# Revit family: Domotics-DomesticRanges-GEWISS-CHORUS_COMMAND-TWO-WAY_SWITCH_3M
name_source: partatom
category: Apparecchi elettrici
revit_build: Autodesk Revit 2016 (Build: 20161004_0715(x64)
units: mm (PartAtom-declared; Revit-internal decimal feet)

## family parameters
Condiviso = Sì
Host = Superficie
Mantenere orientamento annotazione = Sì
Numero OmniClass = 23.80.50.11.14
Punto di calcolo locali = No
Quota connettore circolare = Usa diametro
Taglio con vuoti quando caricato = Sì
Tipo di parte = Normale
Titolo OmniClass = Switches

## types (9) — shared parameters
Bidimensionale = bidimensionale deviatori 3m : GW12083
Breaking capacity: = 1.25 In (200 position changes)
Carico apparente = 0 VA
Catalogue = DOMOTICS
Catalogue Range = CHORUS - DOMESTIC RANGE
Category = Two-way switch
Electrocod = 0130
Glow Wire Test = 850°C
IDF = d9a2dc52-6f96-4b1c-9b7b-49a30463d75b
IDT = d1057cd6-66b4-4a20-be77-f6946e40f1f8
Immagine tipo = GW14083.jpg
Insulation resistance = > 5 MOhm
Larghezza pulsante = 69 mm  [stored 0.226378 ft]
N. poli = 1
No. Chorus modules = 3
Number of poles = 1P
Produttore = GEWISS S.p.A.
Prolonged operation (no.of position changes) = 40.000 at In 250 V ac cosÃ˜=0,6
Prospetto di default = 1219 mm
Resistance at test voltage = 2000 V at 50 Hz for 1 minute
SEO = 2 way switch
Simbolo = SIMBOLO DEVIATORI : DEV1PLUM
Standard; = EN 60669-1
Technical sheet = https://www.gewiss.com
Terminal grip on cable traction = > 50 N
Terminal tightening capacity flexible cables (mm2) = min. 0,75 - max. 2x4
Terminal tightening capacity rigid cables (mm2) = min. 0,5 - max. 2x2,5
Thermo-pressure with ball = 125
Tipo_ = CHORUS DEVIATORI 3M_BASE : GW14083 - Titanio - Illuminabile segnalazione
URL = https://www.gewiss.com
Version file RFA = 19.0
Volt = 230 V
Voltage = 250 V ac
Voltage: = 250 V ac
Wiring terminals = With screw

## per-type parameters (varying)
| type | Button key | Colour | Description: | Descrizione | EAN code | Modello | Type |
| GW10083 - White - Illuminable | With replaceable neutral lens | White | 1P - 16AX illuminable | 2-WAY SWITCH, 3M 1P 16AX ILL SIG WHITE | 8011564257474 | GW10083 | Indicator |
| GW12083 - Black - Illuminable | With replaceable neutral lens | Black | 1P - 16AX illuminable | 2-WAY SWITCH, 3M 1P 16AX ILL SIG BLACK | 8011564268456 | GW12083 | Indicator |
| GW12082 - Black - Illuminable | With diffuser | Black | 1P - 16AX illuminable | 2-WAY SWITCH, 3M 1P 16AX ILL LOC BLACK | 8011564268449 | GW12082 | Backlit |
| GW14083 - Titanium - Illuminable | With replaceable neutral lens | Titanium | 1P - 16AX illuminable | 2-WAY SWITCH 3M 1P 16AX ILL SIG TITANIUM | 8011564265691 | GW14083 | Indicator |
| GW10081 - White | Neutral | White | 1P - 16AX | 2-WAY SWITCH, 3M 1P 16AX WHITE | 8011564257450 | GW10081 | General |
| GW12081 - Black | Neutral | Black | 1P - 16AX | 2-WAY SWITCH, 3M 1P 16AX BLACK | 8011564268425 | GW12081 | General |
| GW14081 - Titanium | Neutral | Titanium | 1P - 16AX | 2-WAY SWITCH, 3M 1P 16AX TITANIUM | 8011564265660 | GW14081 | General |
| GW10082 - White - Illuminable | With diffuser | White | 1P - 16AX illuminable | 2-WAY SWITCH, 3M 1P 16AX ILL LOC WHITE | 8011564257467 | GW10082 | Backlit |
| GW14082 - Titanium - Illuminable | With diffuser | Titanium | 1P - 16AX illuminable | 2-WAY SWITCH 3M 1P 16AX ILL LOC TITANIUM | 8011564265677 | GW14082 | Backlit |

note: source unit labels omitted for Thermo-pressure with ball — the stored unit's dimension contradicts the parameter name (converter mislabeling)

note: [stored X ft] marks values corroborated as IEEE doubles in the binary element streams (Revit-internal decimal feet)

## geometry (parser evidence)
native form markers: Sweep x2
no freeform markers — native parametric forms only
